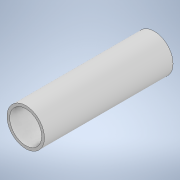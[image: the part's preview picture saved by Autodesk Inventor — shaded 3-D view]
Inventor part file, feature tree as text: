
AUTODESK INVENTOR PART (.ipt)
format: ipt  version: 2022.2 (Build 262287000, 287)  size: 96,768 bytes
history: native  units: in
note: dims shown in document units (in); Inventor stores cm internally (conversion verified against a paired STEP export)
features: extrude x1, sketch x1
ambient origin geometry x8: Origin, YZ Plane, XZ Plane, XY Plane, X Axis, Y Axis, Z Axis, Center Point
bodies: Solid1 (feature_tree)
feature tree (2):
  extrude  "Extrusion1"  Depth=12.0in
  sketch  "Sketch1"  dims[d0=3.5in d1=2.988in d2=12.0in d3=0.0in]
